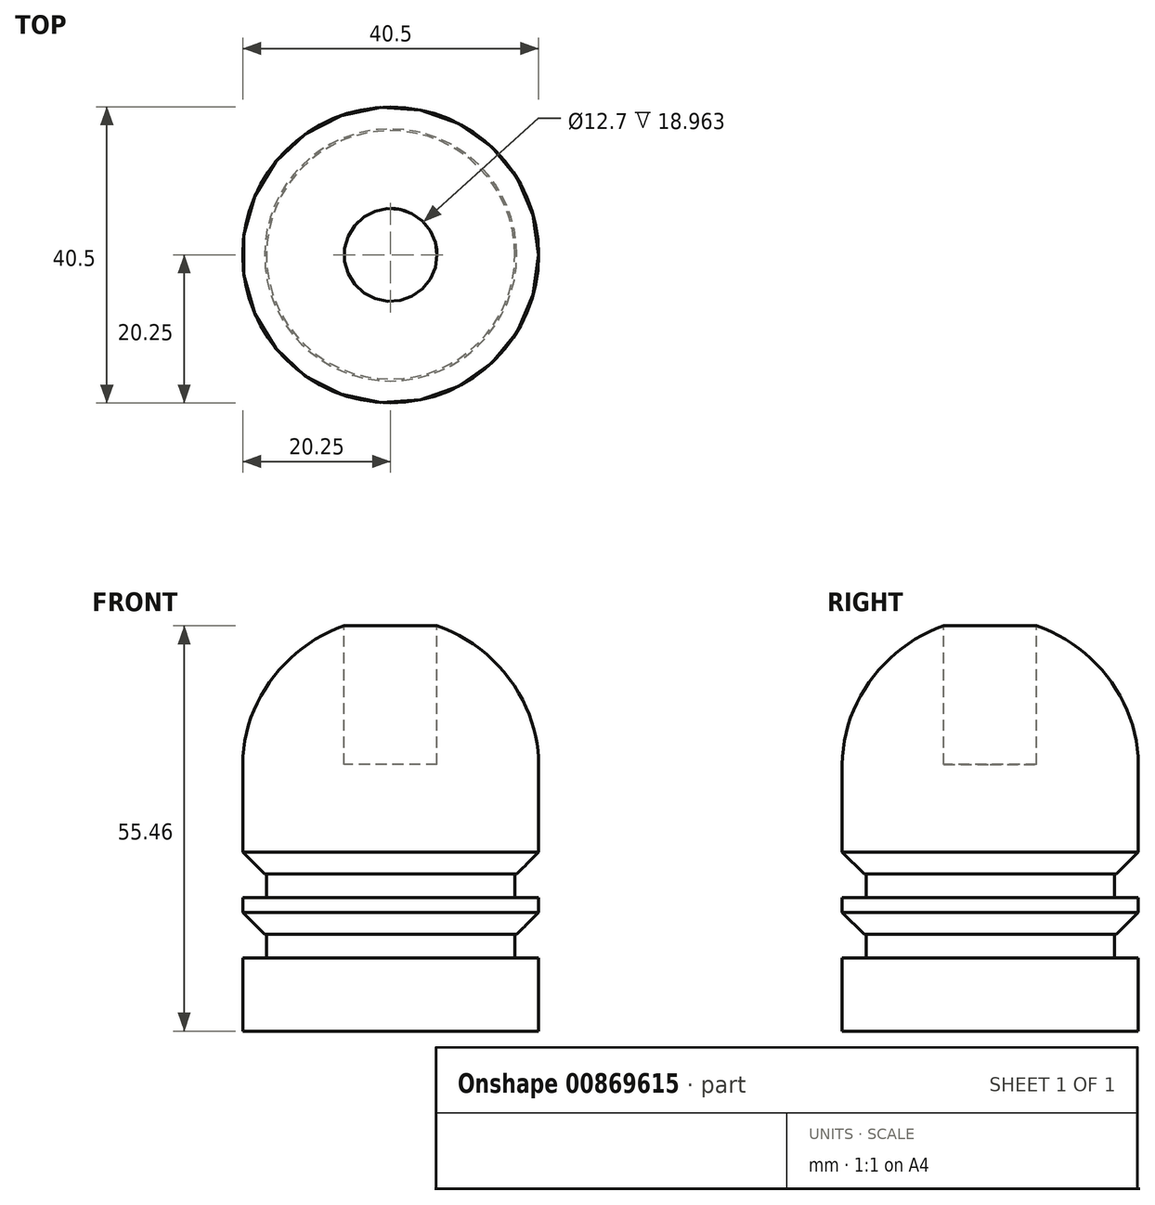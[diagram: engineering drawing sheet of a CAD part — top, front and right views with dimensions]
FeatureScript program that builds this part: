
annotation { "Feature Type Name" : "Feature", "Feature Type Description" : "" }
export const myFeature = defineFeature(function(context is Context, id is Id, definition is map)
    precondition{}
    {
        {
            var Q0;
            Q0=qCreatedBy(makeId("Top.planeOp"),FACE);
            var sketch = newSketch(context, id + "F0", { "sketchPlane" : qUnion([Q0])});
            skCircle(sketch, "E0", {"center": v(0, 0) * mm, "radius": 20.25 * mm});
            skSolve(sketch);
        }
        {
            var Q0;
            Q0 = qSketchRegion(id + "F0", true);
            extrude(context, id + "F1", {"entities" : qUnion([Q0]), "depth" : 10 * mm, "offsetDistance" : 25 * mm});
        }
        {
            var Q0;
            Q0=makeQuery(id+"F1.opExtrude","CAP_FACE",FACE,{"disambiguationData":[OSD([sQuery(id+"F0.wireOp",EDGE,"E0")])],"isStart":false});
            var sketch = newSketch(context, id + "F2", { "sketchPlane" : qUnion([Q0])});
            skCircle(sketch, "E1", {"center": v(0, 0) * mm, "radius": 17 * mm});
            skSolve(sketch);
        }
        {
            var Q0;
            Q0 = qSketchRegion(id + "F2", true);
            extrude(context, id + "F3", {"entities" : qUnion([Q0]), "operationType" : NewBodyOperationType.ADD, "depth" : 3.25 * mm, "offsetDistance" : 25 * mm});
        }
        {
            var Q0;
            Q0=makeQuery(id+"F3.opExtrude","CAP_FACE",FACE,{"disambiguationData":[OSD([sQuery(id+"F2.wireOp",EDGE,"E1")])],"isStart":false});
            var sketch = newSketch(context, id + "F4", { "sketchPlane" : qUnion([Q0])});
            skCircle(sketch, "E2", {"center": v(0, 0) * mm, "radius": 20.25 * mm});
            skSolve(sketch);
        }
        {
            var Q0;
            Q0=makeQuery(id+"F4.imprint","IMPRINT",FACE,{"disambiguationData":[TD([[makeQuery(id+"F4.imprint","IMPRINT",EDGE,{"derivedFrom":makeQuery(id+"F3.opExtrude","CAP_EDGE",EDGE,{"disambiguationData":[OSD([sQuery(id+"F2.wireOp",EDGE,"E1")])],"isStart":false})}),1.0]])]});
            var Q1;
            Q1=makeQuery(id+"F4.imprint","IMPRINT",FACE,{"disambiguationData":[TD([[makeQuery(id+"F4.imprint","IMPRINT",EDGE,{"derivedFrom":sQuery(id+"F4.wireOp",EDGE,"E2")}),1.0]])]});
            extrude(context, id + "F5", {"entities" : qUnion([Q0, Q1]), "operationType" : NewBodyOperationType.ADD, "depth" : 5 * mm, "offsetDistance" : 25 * mm});
        }
        {
            var Q0;
            Q0=makeQuery(id+"F5.opExtrude","CAP_FACE",FACE,{"disambiguationData":[OSD([sQuery(id+"F4.wireOp",EDGE,"E2")])],"isStart":false});
            var sketch = newSketch(context, id + "F6", { "sketchPlane" : qUnion([Q0])});
            skCircle(sketch, "E3", {"center": v(0, 0) * mm, "radius": 17 * mm});
            skSolve(sketch);
        }
        {
            var Q0;
            Q0 = qSketchRegion(id + "F6", true);
            extrude(context, id + "F7", {"entities" : qUnion([Q0]), "operationType" : NewBodyOperationType.ADD, "depth" : 3.25 * mm, "offsetDistance" : 25 * mm});
        }
        {
            var Q0;
            Q0=makeQuery(id+"F7.opExtrude","CAP_FACE",FACE,{"disambiguationData":[OSD([sQuery(id+"F6.wireOp",EDGE,"E3")])],"isStart":false});
            var sketch = newSketch(context, id + "F8", { "sketchPlane" : qUnion([Q0])});
            skCircle(sketch, "E4", {"center": v(0, 0) * mm, "radius": 20.25 * mm});
            skSolve(sketch);
        }
        {
            var Q0;
            Q0=makeQuery(id+"F8.imprint","IMPRINT",FACE,{"disambiguationData":[TD([[makeQuery(id+"F8.imprint","IMPRINT",EDGE,{"derivedFrom":sQuery(id+"F8.wireOp",EDGE,"E4")}),1.0]])]});
            var Q1;
            Q1=makeQuery(id+"F8.imprint","IMPRINT",FACE,{"disambiguationData":[TD([[makeQuery(id+"F8.imprint","IMPRINT",EDGE,{"derivedFrom":makeQuery(id+"F7.opExtrude","CAP_EDGE",EDGE,{"disambiguationData":[OSD([sQuery(id+"F6.wireOp",EDGE,"E3")])],"isStart":false})}),1.0]])]});
            extrude(context, id + "F9", {"entities" : qUnion([Q0, Q1]), "operationType" : NewBodyOperationType.ADD, "depth" : 25 * mm, "offsetDistance" : 25 * mm});
        }
        {
            var Q0;
            Q0=makeQuery(id+"F9.opExtrude","CAP_FACE",FACE,{"disambiguationData":[OSD([sQuery(id+"F8.wireOp",EDGE,"E4")])],"isStart":false});
            extrude(context, id + "F10", {"entities" : qUnion([Q0]), "operationType" : NewBodyOperationType.ADD, "depth" : 5 * mm, "offsetDistance" : 25 * mm});
        }
        {
            var Q0;
            Q0=makeQuery(id+"F10.opExtrude","CAP_FACE",FACE,{"disambiguationData":[OSD([sQuery(id+"F8.wireOp",EDGE,"E4")])],"isStart":false});
            extrude(context, id + "F11", {"entities" : qUnion([Q0]), "operationType" : NewBodyOperationType.ADD, "depth" : 5 * mm, "offsetDistance" : 25 * mm});
        }
        {
            var Q0;
            Q0=makeQuery(id+"F11.opExtrude","CAP_EDGE",EDGE,{"disambiguationData":[OSD([sQuery(id+"F8.wireOp",EDGE,"E4")])],"isStart":false});
            fillet(context, id + "F12", {"entities" : qUnion([Q0]), "radius" : 20 * mm, "tangentPropagation" : true, "rho" : .4, "crossSection" : FilletCrossSection.CONIC, "allowEdgeOverflow" : false});
        }
        {
            var Q0;
            Q0=makeQuery(id+"F11.opExtrude","CAP_FACE",FACE,{"disambiguationData":[OSD([sQuery(id+"F8.wireOp",EDGE,"E4")])],"isStart":false});
            var sketch = newSketch(context, id + "F13", { "sketchPlane" : qUnion([Q0])});
            skCircle(sketch, "E5", {"center": v(0, 0) * mm, "radius": 6.35 * mm});
            skSolve(sketch);
        }
        {
            var Q0;
            Q0=makeQuery(id+"F13.imprint","IMPRINT",FACE,{"disambiguationData":[TD([[makeQuery(id+"F13.imprint","IMPRINT",EDGE,{"derivedFrom":sQuery(id+"F13.wireOp",EDGE,"E5")}),1.0]])]});
            var Q1;
            {var subQ0=sQuery(id+"F8.wireOp",EDGE,"E4");Q1=makeQuery(id+"F13.imprint","IMPRINT",FACE,{"disambiguationData":[TD([[makeQuery(id+"F13.imprint","IMPRINT",EDGE,{"derivedFrom":makeQuery(id+"F12.opFillet","BLEND_EDGE",EDGE,{"blendedFrom":[makeQuery(id+"F11.opExtrude","CAP_EDGE",EDGE,{"disambiguationData":[OSD([subQ0])],"isStart":false}),makeQuery(id+"F11.opExtrude","CAP_FACE",FACE,{"disambiguationData":[OSD([subQ0])],"isStart":false})],"blendedInto":[makeQuery(id+"F11.opExtrude","CAP_FACE",FACE,{"disambiguationData":[OSD([subQ0])],"isStart":false})]})}),1.0]])]});}
            extrude(context, id + "F14", {"entities" : qUnion([Q0, Q1]), "operationType" : NewBodyOperationType.REMOVE, "oppositeDirection" : true, "depth" : 20 * mm, "offsetDistance" : 25 * mm});
        }
        {
            var Q0;
            Q0=makeQuery(id+"F5.opExtrude","CAP_EDGE",EDGE,{"disambiguationData":[OSD([sQuery(id+"F4.wireOp",EDGE,"E2")])],"isStart":true});
            var Q1;
            Q1=makeQuery(id+"F9.opExtrude","CAP_EDGE",EDGE,{"disambiguationData":[OSD([sQuery(id+"F8.wireOp",EDGE,"E4")])],"isStart":true});
            chamfer(context, id + "F15", {"entities" : qUnion([Q0, Q1]), "width" : 3 * mm, "tangentPropagation" : true});
        }
    });
